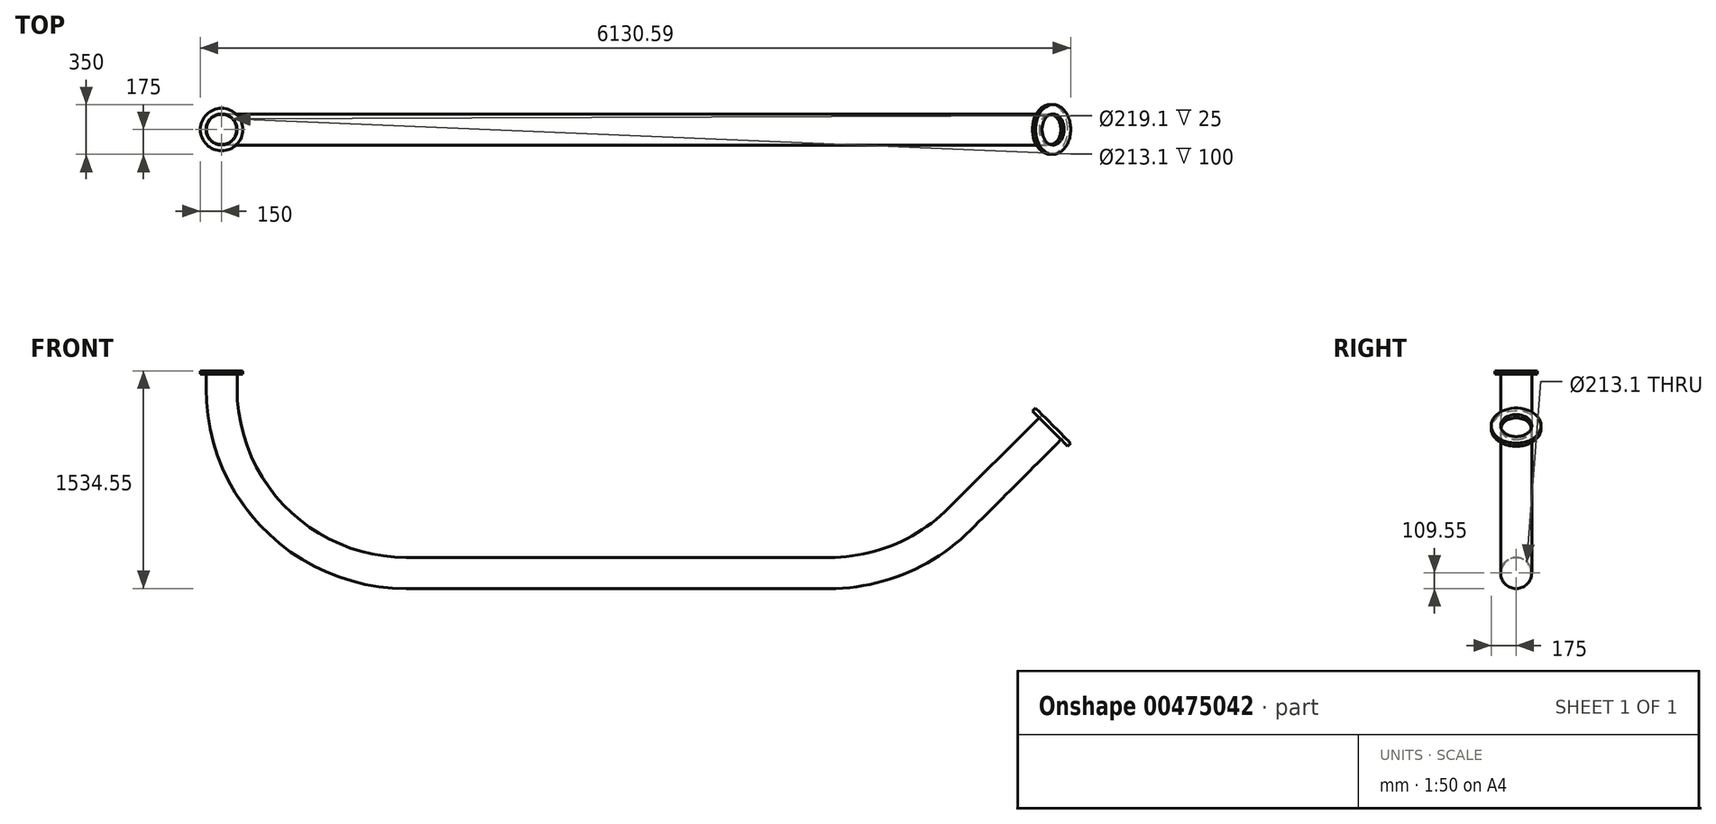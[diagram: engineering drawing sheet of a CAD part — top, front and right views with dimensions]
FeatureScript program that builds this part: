
annotation { "Feature Type Name" : "Feature", "Feature Type Description" : "" }
export const myFeature = defineFeature(function(context is Context, id is Id, definition is map)
    precondition{}
    {
        {
            var Q0;
            Q0=qCreatedBy(makeId("Front.planeOp"),FACE);
            var sketch = newSketch(context, id + "F0", { "sketchPlane" : qUnion([Q0])});
            skLineSegment(sketch, "E0", {"start": v(-1490, 0) * mm, "end": v(1490, 0) * mm, "construction": true});
            skArc(sketch, "E1", {"start": v(-1490, 0) * mm, "mid": v(-2409.24, 380.76) * mm, "end": v(-2790, 1300) * mm, "construction": true});
            skPoint(sketch, "E2", {"position": v(0, 0) * mm});
            skArc(sketch, "E3.5", {"start": v(-1490, -109.55) * mm, "mid": v(-2486.7, 303.3) * mm, "end": v(-2899.55, 1300) * mm});
            skLineSegment(sketch, "E3.6", {"start": v(-1490, -109.55) * mm, "end": v(1490, -109.55) * mm});
            skLineSegment(sketch, "E4", {"start": v(-1490, 0) * mm, "end": v(-1490, -109.55) * mm});
            skLineSegment(sketch, "E5", {"start": v(-2899.55, 1300) * mm, "end": v(-2790, 1300) * mm});
            skLineSegment(sketch, "E6", {"start": v(0, 0) * mm, "end": v(0, -109.55) * mm, "construction": true});
            skLineSegment(sketch, "E7.MirrorCS", {"start": v(1490, 0) * mm, "end": v(1490, -109.55) * mm});
            skLineSegment(sketch, "E8", {"start": v(-2790, 1300) * mm, "end": v(-2790, 1400) * mm, "construction": true});
            skLineSegment(sketch, "E9", {"start": v(-2790, 1400) * mm, "end": v(-2899.55, 1400) * mm});
            skLineSegment(sketch, "E10", {"start": v(-2899.55, 1400) * mm, "end": v(-2899.55, 1300) * mm});
            skLineSegment(sketch, "E11.bottom", {"start": v(2622.6, -159.55) * mm, "end": v(-2577.4, -159.55) * mm, "construction": true});
            skLineSegment(sketch, "E11.top", {"start": v(3022.6, 540.45) * mm, "end": v(-2977.4, 540.45) * mm, "construction": true});
            skLineSegment(sketch, "E11.left", {"start": v(3022.6, 340.45) * mm, "end": v(3022.6, 540.45) * mm, "construction": true});
            skLineSegment(sketch, "E11.right", {"start": v(-2977.4, 340.45) * mm, "end": v(-2977.4, 540.45) * mm, "construction": true});
            skLineSegment(sketch, "E12", {"start": v(-2977.4, 340.45) * mm, "end": v(-2577.4, -159.55) * mm, "construction": true});
            skLineSegment(sketch, "E13", {"start": v(2622.6, -159.55) * mm, "end": v(3022.6, 340.45) * mm, "construction": true});
            skPoint(sketch, "E14", {"position": v(22.6, -159.55) * mm});
            skLineSegment(sketch, "E15", {"start": v(-2677.4, 540.45) * mm, "end": v(-2677.4, -34.55) * mm, "construction": true});
            skLineSegment(sketch, "E16", {"start": v(-2677.4, 540.45) * mm, "end": v(-2277.4, 40.45) * mm});
            skLineSegment(sketch, "E17", {"start": v(2723.85, 540.45) * mm, "end": v(2723.85, -32.98) * mm, "construction": true});
            skArc(sketch, "E18", {"start": v(1490, 0) * mm, "mid": v(1987.49, 98.96) * mm, "end": v(2409.24, 380.76) * mm, "construction": true});
            skArc(sketch, "E19", {"start": v(1490, -109.55) * mm, "mid": v(2029.41, -2.25) * mm, "end": v(2486.7, 303.3) * mm});
            skLineSegment(sketch, "E20", {"start": v(2409.24, 380.76) * mm, "end": v(2486.7, 303.3) * mm});
            skLineSegment(sketch, "E21", {"start": v(2486.7, 303.3) * mm, "end": v(3123.1, 939.7) * mm});
            skLineSegment(sketch, "E22", {"start": v(3123.1, 939.7) * mm, "end": v(3045.63, 1017.16) * mm});
            skLineSegment(sketch, "E23", {"start": v(3045.63, 1017.16) * mm, "end": v(2409.24, 380.76) * mm, "construction": true});
            skSolve(sketch);
        }
        {
            var Q0;
            Q0=qCreatedBy(makeId("Front.planeOp"),FACE);
            var sketch = newSketch(context, id + "F1", { "sketchPlane" : qUnion([Q0])});
            skLineSegment(sketch, "E24", {"start": v(-2896.55, 1400) * mm, "end": v(-2896.55, 1300) * mm});
            skLineSegment(sketch, "E25", {"start": v(-2899.55, 1400) * mm, "end": v(-2896.55, 1400) * mm});
            skLineSegment(sketch, "E26", {"start": v(-2899.55, 1300) * mm, "end": v(-2896.55, 1300) * mm});
            skLineSegment(sketch, "E27", {"start": v(-2899.55, 1300) * mm, "end": v(-2899.55, 1400) * mm});
            skSolve(sketch);
        }
        {
            var Q0;
            Q0=makeQuery(id+"F1.imprint","IMPRINT",FACE,{"disambiguationData":[TD([[makeQuery(id+"F1.imprint","IMPRINT",EDGE,{"derivedFrom":sQuery(id+"F1.wireOp",EDGE,"E24")}),-1.0]])]});
            var Q1;
            Q1=sQuery(id+"F0.wireOp",EDGE,"E8");
            revolve(context, id + "F2", {"entities" : qUnion([Q0]), "axis" : qUnion([Q1]), "revolveType" : RevolveType.FULL});
        }
        {
            var Q0;
            Q0=makeQuery(id+"F2.opRevolve","SWEPT_FACE",FACE,{"disambiguationData":[OSD([sQuery(id+"F1.wireOp",EDGE,"E26")])]});
            var Q1;
            Q1=sQuery(id+"F0.wireOp",EDGE,"E3.3");
            var Q2;
            Q2=sQuery(id+"F0.wireOp",EDGE,"ehUSYPVM-8In4-UokY-o1ir-dxswM0NRwGns");
            var Q3;
            Q3=sQuery(id+"F0.wireOp",EDGE,"E3.5");
            var Q4;
            Q4=sQuery(id+"F0.wireOp",EDGE,"E3.6");
            var Q5;
            Q5=sQuery(id+"F0.wireOp",EDGE,"d5dcd199-87a5-43e9-9218-31ebdbec5ac011.MirrorCS");
            var Q6;
            Q6=sQuery(id+"F0.wireOp",EDGE,"d5dcd199-87a5-43e9-9218-31ebdbec5ac07.MirrorCS");
            var Q7;
            Q7=sQuery(id+"F0.wireOp",EDGE,"d5dcd199-87a5-43e9-9218-31ebdbec5ac03.MirrorCS");
            var Q8;
            Q8=sQuery(id+"F0.wireOp",EDGE,"d5dcd199-87a5-43e9-9218-31ebdbec5ac09.MirrorCS");
            var Q9;
            Q9=sQuery(id+"F0.wireOp",EDGE,"913ca05b-7b36-42bc-a168-2c98df43f88b0.MirrorCS");
            sweep(context, id + "F3", {"operationType" : NewBodyOperationType.ADD, "profiles" : qUnion([Q0]), "path" : qUnion([Q1, Q2, Q3, Q4, Q5, Q6, Q7, Q8, Q9])});
        }
        {
            var Q0;
            Q0=makeQuery(id+"F3.opSweep","CAP_FACE",FACE,{"disambiguationData":[OSD([sQuery(id+"F0.wireOp",VERTEX,"E3.6.end"),dummyQuery(id+"FcjeWj101vwSLZw_0.vertexPlane.planeOp",FACE)])],"isStart":false});
            var Q1;
            Q1=sQuery(id+"F0.wireOp",EDGE,"E19");
            var Q2;
            Q2=sQuery(id+"F0.wireOp",EDGE,"E21");
            sweep(context, id + "F4", {"operationType" : NewBodyOperationType.ADD, "profiles" : qUnion([Q0]), "path" : qUnion([Q1, Q2])});
        }
        {
            var Q0;
            Q0=makeQuery(id+"F2.opRevolve","SWEPT_FACE",FACE,{"disambiguationData":[OSD([sQuery(id+"F1.wireOp",EDGE,"E25")])]});
            var sketch = newSketch(context, id + "F5", { "sketchPlane" : qUnion([Q0])});
            skCircle(sketch, "E28", {"center": v(-2790, 0) * mm, "radius": 150 * mm});
            skCircle(sketch, "E29", {"center": v(-2790, 0) * mm, "radius": 109.55 * mm});
            skSolve(sketch);
        }
        {
            var Q0;
            Q0=makeQuery(id+"F5.imprint","IMPRINT",FACE,{"disambiguationData":[TD([[makeQuery(id+"F5.imprint","IMPRINT",EDGE,{"derivedFrom":sQuery(id+"F5.wireOp",EDGE,"E28")}),1.0]])]});
            var Q1;
            Q1=makeQuery(id+"F5.imprint","IMPRINT",FACE,{"disambiguationData":[TD([[makeQuery(id+"F5.imprint","IMPRINT",EDGE,{"derivedFrom":sQuery(id+"F5.wireOp",EDGE,"y8ymGNpF-K1WR-XcHZ-xaFE-vk0SO8xZg14S")}),1.0]])]});
            var Q2;
            Q2=sQuery(id+"F5.wireOp",EDGE,"E28");
            extrude(context, id + "F6", {"entities" : qUnion([Q0, Q1]), "surfaceEntities" : qUnion([Q2]), "depth" : 25 * mm});
        }
        {
            var Q0;
            Q0=makeQuery(id+"F4.opSweep","CAP_FACE",FACE,{"disambiguationData":[OSD([sQuery(id+"F0.wireOp",VERTEX,"E3.6.end"),sQuery(id+"F0.wireOp",VERTEX,"E21.end"),dummyQuery(id+"FcjeWj101vwSLZw_0.vertexPlane.planeOp",FACE)])],"isStart":false});
            var sketch = newSketch(context, id + "F7", { "sketchPlane" : qUnion([Q0])});
            skCircle(sketch, "E30", {"center": v(0, -1434.35) * mm, "radius": 175 * mm});
            skCircle(sketch, "E31", {"center": v(0, -1434.35) * mm, "radius": 106.55 * mm});
            skSolve(sketch);
        }
        {
            var Q0;
            Q0=makeQuery(id+"F7.imprint","IMPRINT",FACE,{"disambiguationData":[TD([[makeQuery(id+"F7.imprint","IMPRINT",EDGE,{"derivedFrom":sQuery(id+"F7.wireOp",EDGE,"E30")}),1.0]])]});
            extrude(context, id + "F8", {"entities" : qUnion([Q0]), "depth" : 30 * mm});
        }
    });
